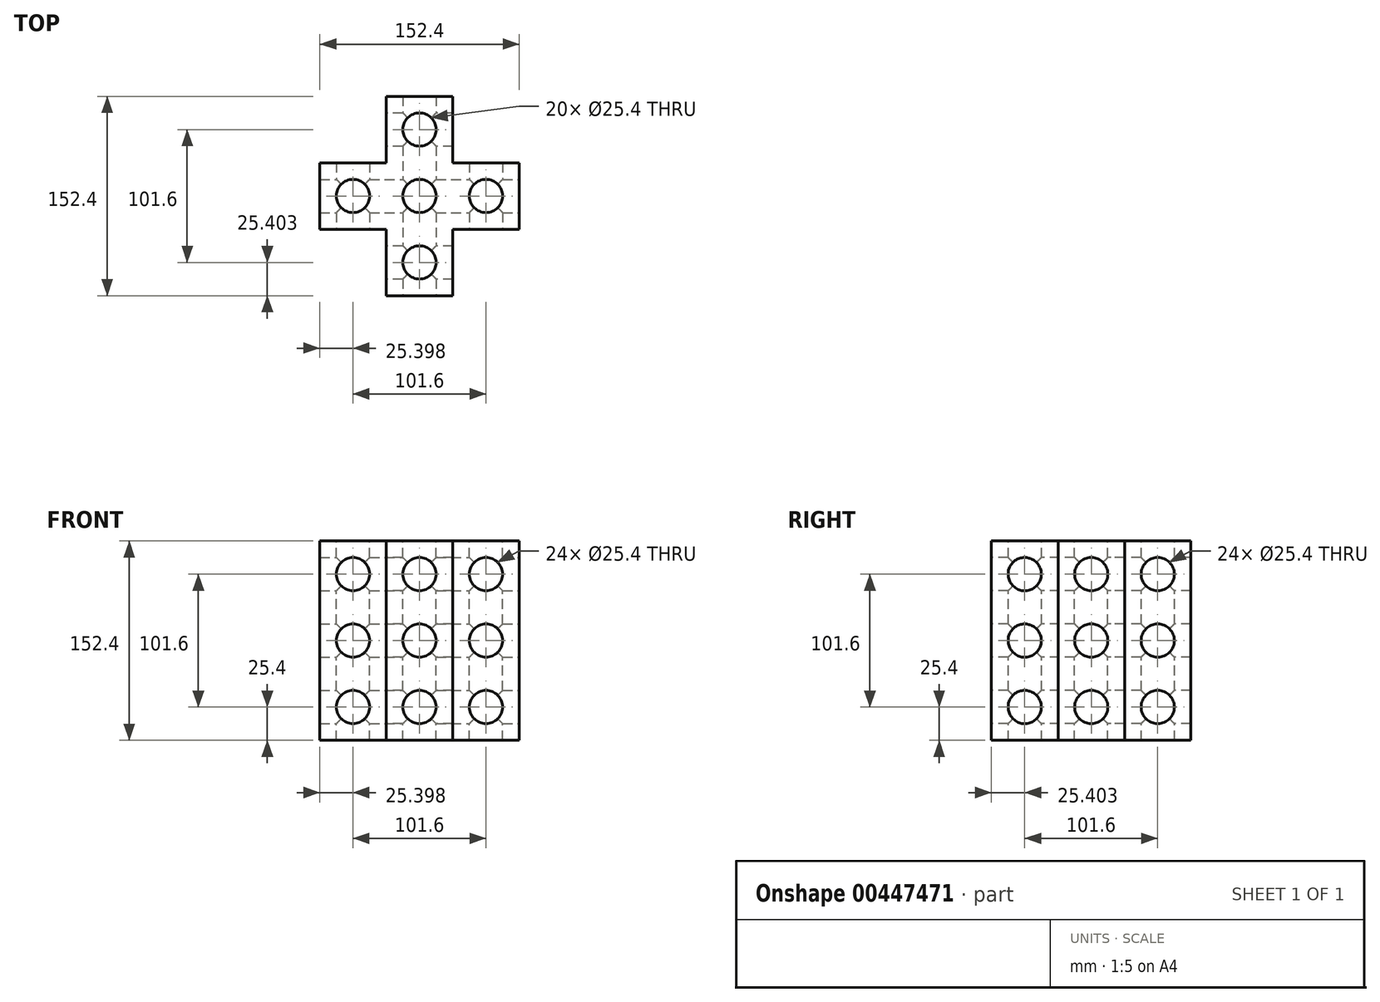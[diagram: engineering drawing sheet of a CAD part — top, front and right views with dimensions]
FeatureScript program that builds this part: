
annotation { "Feature Type Name" : "Feature", "Feature Type Description" : "" }
export const myFeature = defineFeature(function(context is Context, id is Id, definition is map)
    precondition{}
    {
        {
            var Q0;
            Q0=qCreatedBy(makeId("Top.planeOp"),FACE);
            var sketch = newSketch(context, id + "F0", { "sketchPlane" : qUnion([Q0])});
            skLineSegment(sketch, "E0", {"start": v(14.3, 102.3) * mm, "end": v(-36.5, 102.3) * mm});
            skLineSegment(sketch, "E1", {"start": v(-36.5, 102.3) * mm, "end": v(-36.5, 51.5) * mm});
            skLineSegment(sketch, "E2", {"start": v(-36.5, 51.5) * mm, "end": v(-87.3, 51.5) * mm});
            skLineSegment(sketch, "E3", {"start": v(-87.3, 51.5) * mm, "end": v(-87.3, 0.7) * mm});
            skLineSegment(sketch, "E4", {"start": v(-87.3, 0.7) * mm, "end": v(-36.5, 0.7) * mm});
            skLineSegment(sketch, "E5", {"start": v(-36.5, 0.7) * mm, "end": v(-36.5, -50.1) * mm});
            skLineSegment(sketch, "E6", {"start": v(-36.5, -50.1) * mm, "end": v(14.3, -50.1) * mm});
            skLineSegment(sketch, "E7", {"start": v(14.3, -50.1) * mm, "end": v(14.3, 0.7) * mm});
            skLineSegment(sketch, "E8", {"start": v(14.3, 0.7) * mm, "end": v(65.1, 0.7) * mm});
            skLineSegment(sketch, "E9", {"start": v(65.1, 0.7) * mm, "end": v(65.1, 51.5) * mm});
            skLineSegment(sketch, "E10", {"start": v(65.1, 51.5) * mm, "end": v(14.3, 51.5) * mm});
            skLineSegment(sketch, "E11", {"start": v(14.3, 51.5) * mm, "end": v(14.3, 102.3) * mm});
            skSolve(sketch);
        }
        {
            var Q0;
            Q0 = qSketchRegion(id + "F0", true);
            extrude(context, id + "F1", {"entities" : qUnion([Q0]), "depth" : 152.4 * mm});
        }
        {
            var Q0;
            Q0=makeQuery(id+"F1.opExtrude","SWEPT_FACE",FACE,{"disambiguationData":[OSD([sQuery(id+"F0.wireOp",EDGE,"E6")])]});
            var sketch = newSketch(context, id + "F2", { "sketchPlane" : qUnion([Q0])});
            skCircle(sketch, "E12", {"center": v(-11.1, 127) * mm, "radius": 12.7 * mm});
            skCircle(sketch, "E13", {"center": v(-11.1, 76.2) * mm, "radius": 12.7 * mm});
            skCircle(sketch, "E14", {"center": v(-11.1, 25.4) * mm, "radius": 12.7 * mm});
            skSolve(sketch);
        }
        {
            var Q0;
            Q0=sQuery(id+"F2.wireOp",VERTEX,"E12.center");
            var Q1;
            Q1=makeQuery(id+"F1.opExtrude","SWEPT_BODY",BODY,{"disambiguationData":[OSD([sQuery(id+"F0.wireOp",EDGE,"E0"),sQuery(id+"F0.wireOp",EDGE,"E1"),sQuery(id+"F0.wireOp",EDGE,"E2"),sQuery(id+"F0.wireOp",EDGE,"E3"),sQuery(id+"F0.wireOp",EDGE,"E4"),sQuery(id+"F0.wireOp",EDGE,"E5"),sQuery(id+"F0.wireOp",EDGE,"E6"),sQuery(id+"F0.wireOp",EDGE,"E7"),sQuery(id+"F0.wireOp",EDGE,"E8"),sQuery(id+"F0.wireOp",EDGE,"E9"),sQuery(id+"F0.wireOp",EDGE,"E10"),sQuery(id+"F0.wireOp",EDGE,"E11")])]});
            hole(context, id + "F3", {"style" : HoleStyle.SIMPLE, "endStyle" : HoleEndStyle.THROUGH, "holeDiameter" : 25.4 * mm, "isTappedThrough" : true, "tappedDepth" : 12.7 * mm, "tapClearance" : 3, "locations" : qUnion([Q0]), "scope" : qUnion([Q1])});
        }
        {
            var Q0;
            Q0=makeQuery(id+"F1.opExtrude","SWEPT_FACE",FACE,{"disambiguationData":[OSD([sQuery(id+"F0.wireOp",EDGE,"E6")])]});
            var sketch = newSketch(context, id + "F4", { "sketchPlane" : qUnion([Q0])});
            skCircle(sketch, "E15", {"center": v(-11.1, 76.2) * mm, "radius": 12.7 * mm});
            skSolve(sketch);
        }
        {
            var Q0;
            Q0=sQuery(id+"F4.wireOp",VERTEX,"E15.center");
            var Q1;
            Q1=makeQuery(id+"F1.opExtrude","SWEPT_BODY",BODY,{"disambiguationData":[OSD([sQuery(id+"F0.wireOp",EDGE,"E0"),sQuery(id+"F0.wireOp",EDGE,"E1"),sQuery(id+"F0.wireOp",EDGE,"E2"),sQuery(id+"F0.wireOp",EDGE,"E3"),sQuery(id+"F0.wireOp",EDGE,"E4"),sQuery(id+"F0.wireOp",EDGE,"E5"),sQuery(id+"F0.wireOp",EDGE,"E6"),sQuery(id+"F0.wireOp",EDGE,"E7"),sQuery(id+"F0.wireOp",EDGE,"E8"),sQuery(id+"F0.wireOp",EDGE,"E9"),sQuery(id+"F0.wireOp",EDGE,"E10"),sQuery(id+"F0.wireOp",EDGE,"E11")])]});
            hole(context, id + "F5", {"style" : HoleStyle.SIMPLE, "endStyle" : HoleEndStyle.THROUGH, "holeDiameter" : 25.4 * mm, "isTappedThrough" : true, "tappedDepth" : 12.7 * mm, "tapClearance" : 3, "locations" : qUnion([Q0]), "scope" : qUnion([Q1])});
        }
        {
            var Q0;
            Q0=makeQuery(id+"F1.opExtrude","SWEPT_FACE",FACE,{"disambiguationData":[OSD([sQuery(id+"F0.wireOp",EDGE,"E6")])]});
            var sketch = newSketch(context, id + "F6", { "sketchPlane" : qUnion([Q0])});
            skCircle(sketch, "E16", {"center": v(-11.1, 25.4) * mm, "radius": 12.7 * mm});
            skSolve(sketch);
        }
        {
            var Q0;
            Q0=sQuery(id+"F6.wireOp",VERTEX,"E16.center");
            var Q1;
            Q1=makeQuery(id+"F1.opExtrude","SWEPT_BODY",BODY,{"disambiguationData":[OSD([sQuery(id+"F0.wireOp",EDGE,"E0"),sQuery(id+"F0.wireOp",EDGE,"E1"),sQuery(id+"F0.wireOp",EDGE,"E2"),sQuery(id+"F0.wireOp",EDGE,"E3"),sQuery(id+"F0.wireOp",EDGE,"E4"),sQuery(id+"F0.wireOp",EDGE,"E5"),sQuery(id+"F0.wireOp",EDGE,"E6"),sQuery(id+"F0.wireOp",EDGE,"E7"),sQuery(id+"F0.wireOp",EDGE,"E8"),sQuery(id+"F0.wireOp",EDGE,"E9"),sQuery(id+"F0.wireOp",EDGE,"E10"),sQuery(id+"F0.wireOp",EDGE,"E11")])]});
            hole(context, id + "F7", {"style" : HoleStyle.SIMPLE, "endStyle" : HoleEndStyle.THROUGH, "holeDiameter" : 25.4 * mm, "isTappedThrough" : true, "tappedDepth" : 12.7 * mm, "tapClearance" : 3, "locations" : qUnion([Q0]), "scope" : qUnion([Q1])});
        }
        {
            var Q0;
            Q0=makeQuery(id+"F1.opExtrude","SWEPT_FACE",FACE,{"disambiguationData":[OSD([sQuery(id+"F0.wireOp",EDGE,"E9")])]});
            var sketch = newSketch(context, id + "F8", { "sketchPlane" : qUnion([Q0])});
            skCircle(sketch, "E17", {"center": v(26.1, 127) * mm, "radius": 12.7 * mm});
            skSolve(sketch);
        }
        {
            var Q0;
            Q0=sQuery(id+"F8.wireOp",VERTEX,"E17.center");
            var Q1;
            Q1=makeQuery(id+"F1.opExtrude","SWEPT_BODY",BODY,{"disambiguationData":[OSD([sQuery(id+"F0.wireOp",EDGE,"E0"),sQuery(id+"F0.wireOp",EDGE,"E1"),sQuery(id+"F0.wireOp",EDGE,"E2"),sQuery(id+"F0.wireOp",EDGE,"E3"),sQuery(id+"F0.wireOp",EDGE,"E4"),sQuery(id+"F0.wireOp",EDGE,"E5"),sQuery(id+"F0.wireOp",EDGE,"E6"),sQuery(id+"F0.wireOp",EDGE,"E7"),sQuery(id+"F0.wireOp",EDGE,"E8"),sQuery(id+"F0.wireOp",EDGE,"E9"),sQuery(id+"F0.wireOp",EDGE,"E10"),sQuery(id+"F0.wireOp",EDGE,"E11")])]});
            hole(context, id + "F9", {"style" : HoleStyle.SIMPLE, "endStyle" : HoleEndStyle.THROUGH, "holeDiameter" : 25.4 * mm, "isTappedThrough" : true, "tappedDepth" : 12.7 * mm, "tapClearance" : 3, "locations" : qUnion([Q0]), "scope" : qUnion([Q1])});
        }
        {
            var Q0;
            Q0=makeQuery(id+"F1.opExtrude","SWEPT_FACE",FACE,{"disambiguationData":[OSD([sQuery(id+"F0.wireOp",EDGE,"E9")])]});
            var sketch = newSketch(context, id + "F10", { "sketchPlane" : qUnion([Q0])});
            skCircle(sketch, "E18", {"center": v(26.1, 76.2) * mm, "radius": 12.7 * mm});
            skSolve(sketch);
        }
        {
            var Q0;
            Q0=sQuery(id+"F10.wireOp",VERTEX,"E18.center");
            var Q1;
            Q1=makeQuery(id+"F1.opExtrude","SWEPT_BODY",BODY,{"disambiguationData":[OSD([sQuery(id+"F0.wireOp",EDGE,"E0"),sQuery(id+"F0.wireOp",EDGE,"E1"),sQuery(id+"F0.wireOp",EDGE,"E2"),sQuery(id+"F0.wireOp",EDGE,"E3"),sQuery(id+"F0.wireOp",EDGE,"E4"),sQuery(id+"F0.wireOp",EDGE,"E5"),sQuery(id+"F0.wireOp",EDGE,"E6"),sQuery(id+"F0.wireOp",EDGE,"E7"),sQuery(id+"F0.wireOp",EDGE,"E8"),sQuery(id+"F0.wireOp",EDGE,"E9"),sQuery(id+"F0.wireOp",EDGE,"E10"),sQuery(id+"F0.wireOp",EDGE,"E11")])]});
            hole(context, id + "F11", {"style" : HoleStyle.SIMPLE, "endStyle" : HoleEndStyle.THROUGH, "holeDiameter" : 25.4 * mm, "isTappedThrough" : true, "tappedDepth" : 12.7 * mm, "tapClearance" : 3, "locations" : qUnion([Q0]), "scope" : qUnion([Q1])});
        }
        {
            var Q0;
            Q0=makeQuery(id+"F1.opExtrude","SWEPT_FACE",FACE,{"disambiguationData":[OSD([sQuery(id+"F0.wireOp",EDGE,"E9")])]});
            var sketch = newSketch(context, id + "F12", { "sketchPlane" : qUnion([Q0])});
            skCircle(sketch, "E19", {"center": v(26.1, 25.4) * mm, "radius": 12.7 * mm});
            skSolve(sketch);
        }
        {
            var Q0;
            Q0=sQuery(id+"F12.wireOp",VERTEX,"E19.center");
            var Q1;
            Q1=makeQuery(id+"F1.opExtrude","SWEPT_BODY",BODY,{"disambiguationData":[OSD([sQuery(id+"F0.wireOp",EDGE,"E0"),sQuery(id+"F0.wireOp",EDGE,"E1"),sQuery(id+"F0.wireOp",EDGE,"E2"),sQuery(id+"F0.wireOp",EDGE,"E3"),sQuery(id+"F0.wireOp",EDGE,"E4"),sQuery(id+"F0.wireOp",EDGE,"E5"),sQuery(id+"F0.wireOp",EDGE,"E6"),sQuery(id+"F0.wireOp",EDGE,"E7"),sQuery(id+"F0.wireOp",EDGE,"E8"),sQuery(id+"F0.wireOp",EDGE,"E9"),sQuery(id+"F0.wireOp",EDGE,"E10"),sQuery(id+"F0.wireOp",EDGE,"E11")])]});
            hole(context, id + "F13", {"style" : HoleStyle.SIMPLE, "endStyle" : HoleEndStyle.THROUGH, "holeDiameter" : 25.4 * mm, "isTappedThrough" : true, "tappedDepth" : 12.7 * mm, "tapClearance" : 3, "locations" : qUnion([Q0]), "scope" : qUnion([Q1])});
        }
        {
            var Q0;
            Q0=makeQuery(id+"F1.opExtrude","CAP_FACE",FACE,{"disambiguationData":[OSD([sQuery(id+"F0.wireOp",EDGE,"E0"),sQuery(id+"F0.wireOp",EDGE,"E1"),sQuery(id+"F0.wireOp",EDGE,"E2"),sQuery(id+"F0.wireOp",EDGE,"E3"),sQuery(id+"F0.wireOp",EDGE,"E4"),sQuery(id+"F0.wireOp",EDGE,"E5"),sQuery(id+"F0.wireOp",EDGE,"E6"),sQuery(id+"F0.wireOp",EDGE,"E7"),sQuery(id+"F0.wireOp",EDGE,"E8"),sQuery(id+"F0.wireOp",EDGE,"E9"),sQuery(id+"F0.wireOp",EDGE,"E10"),sQuery(id+"F0.wireOp",EDGE,"E11")])],"isStart":false});
            var sketch = newSketch(context, id + "F14", { "sketchPlane" : qUnion([Q0])});
            skCircle(sketch, "E20", {"center": v(-11.1, 26.1) * mm, "radius": 12.7 * mm});
            skSolve(sketch);
        }
        {
            var Q0;
            Q0=sQuery(id+"F14.wireOp",VERTEX,"E20.center");
            var Q1;
            Q1=makeQuery(id+"F1.opExtrude","SWEPT_BODY",BODY,{"disambiguationData":[OSD([sQuery(id+"F0.wireOp",EDGE,"E0"),sQuery(id+"F0.wireOp",EDGE,"E1"),sQuery(id+"F0.wireOp",EDGE,"E2"),sQuery(id+"F0.wireOp",EDGE,"E3"),sQuery(id+"F0.wireOp",EDGE,"E4"),sQuery(id+"F0.wireOp",EDGE,"E5"),sQuery(id+"F0.wireOp",EDGE,"E6"),sQuery(id+"F0.wireOp",EDGE,"E7"),sQuery(id+"F0.wireOp",EDGE,"E8"),sQuery(id+"F0.wireOp",EDGE,"E9"),sQuery(id+"F0.wireOp",EDGE,"E10"),sQuery(id+"F0.wireOp",EDGE,"E11")])]});
            hole(context, id + "F15", {"style" : HoleStyle.SIMPLE, "endStyle" : HoleEndStyle.THROUGH, "holeDiameter" : 25.4 * mm, "isTappedThrough" : true, "tappedDepth" : 12.7 * mm, "tapClearance" : 3, "locations" : qUnion([Q0]), "scope" : qUnion([Q1])});
        }
        {
            var Q0;
            Q0=makeQuery(id+"F1.opExtrude","CAP_FACE",FACE,{"disambiguationData":[OSD([sQuery(id+"F0.wireOp",EDGE,"E0"),sQuery(id+"F0.wireOp",EDGE,"E1"),sQuery(id+"F0.wireOp",EDGE,"E2"),sQuery(id+"F0.wireOp",EDGE,"E3"),sQuery(id+"F0.wireOp",EDGE,"E4"),sQuery(id+"F0.wireOp",EDGE,"E5"),sQuery(id+"F0.wireOp",EDGE,"E6"),sQuery(id+"F0.wireOp",EDGE,"E7"),sQuery(id+"F0.wireOp",EDGE,"E8"),sQuery(id+"F0.wireOp",EDGE,"E9"),sQuery(id+"F0.wireOp",EDGE,"E10"),sQuery(id+"F0.wireOp",EDGE,"E11")])],"isStart":false});
            var sketch = newSketch(context, id + "F16", { "sketchPlane" : qUnion([Q0])});
            skCircle(sketch, "E21", {"center": v(39.7, 26.1) * mm, "radius": 12.7 * mm});
            skCircle(sketch, "E22", {"center": v(-61.9, 26.1) * mm, "radius": 12.7 * mm});
            skSolve(sketch);
        }
        {
            var Q0;
            Q0=sQuery(id+"F16.wireOp",VERTEX,"E21.center");
            var Q1;
            Q1=sQuery(id+"F16.wireOp",VERTEX,"E22.center");
            var Q2;
            Q2=makeQuery(id+"F1.opExtrude","SWEPT_BODY",BODY,{"disambiguationData":[OSD([sQuery(id+"F0.wireOp",EDGE,"E0"),sQuery(id+"F0.wireOp",EDGE,"E1"),sQuery(id+"F0.wireOp",EDGE,"E2"),sQuery(id+"F0.wireOp",EDGE,"E3"),sQuery(id+"F0.wireOp",EDGE,"E4"),sQuery(id+"F0.wireOp",EDGE,"E5"),sQuery(id+"F0.wireOp",EDGE,"E6"),sQuery(id+"F0.wireOp",EDGE,"E7"),sQuery(id+"F0.wireOp",EDGE,"E8"),sQuery(id+"F0.wireOp",EDGE,"E9"),sQuery(id+"F0.wireOp",EDGE,"E10"),sQuery(id+"F0.wireOp",EDGE,"E11")])]});
            hole(context, id + "F17", {"style" : HoleStyle.SIMPLE, "endStyle" : HoleEndStyle.THROUGH, "holeDiameter" : 25.4 * mm, "isTappedThrough" : true, "tappedDepth" : 12.7 * mm, "tapClearance" : 3, "locations" : qUnion([Q0, Q1]), "scope" : qUnion([Q2])});
        }
        {
            var Q0;
            Q0=makeQuery(id+"F1.opExtrude","SWEPT_FACE",FACE,{"disambiguationData":[OSD([sQuery(id+"F0.wireOp",EDGE,"E8")])]});
            var sketch = newSketch(context, id + "F18", { "sketchPlane" : qUnion([Q0])});
            skCircle(sketch, "E23", {"center": v(39.7, 127) * mm, "radius": 12.7 * mm});
            skCircle(sketch, "E24", {"center": v(39.7, 76.2) * mm, "radius": 12.7 * mm});
            skCircle(sketch, "E25", {"center": v(39.7, 25.4) * mm, "radius": 12.7 * mm});
            skSolve(sketch);
        }
        {
            var Q0;
            Q0=sQuery(id+"F18.wireOp",VERTEX,"E23.center");
            var Q1;
            Q1=sQuery(id+"F18.wireOp",VERTEX,"E24.center");
            var Q2;
            Q2=sQuery(id+"F18.wireOp",VERTEX,"E25.center");
            var Q3;
            Q3=makeQuery(id+"F1.opExtrude","SWEPT_BODY",BODY,{"disambiguationData":[OSD([sQuery(id+"F0.wireOp",EDGE,"E0"),sQuery(id+"F0.wireOp",EDGE,"E1"),sQuery(id+"F0.wireOp",EDGE,"E2"),sQuery(id+"F0.wireOp",EDGE,"E3"),sQuery(id+"F0.wireOp",EDGE,"E4"),sQuery(id+"F0.wireOp",EDGE,"E5"),sQuery(id+"F0.wireOp",EDGE,"E6"),sQuery(id+"F0.wireOp",EDGE,"E7"),sQuery(id+"F0.wireOp",EDGE,"E8"),sQuery(id+"F0.wireOp",EDGE,"E9"),sQuery(id+"F0.wireOp",EDGE,"E10"),sQuery(id+"F0.wireOp",EDGE,"E11")])]});
            hole(context, id + "F19", {"style" : HoleStyle.SIMPLE, "endStyle" : HoleEndStyle.THROUGH, "holeDiameter" : 25.4 * mm, "isTappedThrough" : true, "tappedDepth" : 12.7 * mm, "tapClearance" : 3, "locations" : qUnion([Q0, Q1, Q2]), "scope" : qUnion([Q3])});
        }
        {
            var Q0;
            Q0=makeQuery(id+"F1.opExtrude","SWEPT_FACE",FACE,{"disambiguationData":[OSD([sQuery(id+"F0.wireOp",EDGE,"E4")])]});
            var sketch = newSketch(context, id + "F20", { "sketchPlane" : qUnion([Q0])});
            skCircle(sketch, "E26", {"center": v(-61.9, 127) * mm, "radius": 12.7 * mm});
            skCircle(sketch, "E27", {"center": v(-61.9, 76.2) * mm, "radius": 12.7 * mm});
            skCircle(sketch, "E28", {"center": v(-61.9, 25.4) * mm, "radius": 12.7 * mm});
            skSolve(sketch);
        }
        {
            var Q0;
            Q0=sQuery(id+"F20.wireOp",VERTEX,"E26.center");
            var Q1;
            Q1=sQuery(id+"F20.wireOp",VERTEX,"E27.center");
            var Q2;
            Q2=sQuery(id+"F20.wireOp",VERTEX,"E28.center");
            var Q3;
            Q3=makeQuery(id+"F1.opExtrude","SWEPT_BODY",BODY,{"disambiguationData":[OSD([sQuery(id+"F0.wireOp",EDGE,"E0"),sQuery(id+"F0.wireOp",EDGE,"E1"),sQuery(id+"F0.wireOp",EDGE,"E2"),sQuery(id+"F0.wireOp",EDGE,"E3"),sQuery(id+"F0.wireOp",EDGE,"E4"),sQuery(id+"F0.wireOp",EDGE,"E5"),sQuery(id+"F0.wireOp",EDGE,"E6"),sQuery(id+"F0.wireOp",EDGE,"E7"),sQuery(id+"F0.wireOp",EDGE,"E8"),sQuery(id+"F0.wireOp",EDGE,"E9"),sQuery(id+"F0.wireOp",EDGE,"E10"),sQuery(id+"F0.wireOp",EDGE,"E11")])]});
            hole(context, id + "F21", {"style" : HoleStyle.SIMPLE, "endStyle" : HoleEndStyle.THROUGH, "holeDiameter" : 25.4 * mm, "isTappedThrough" : true, "tappedDepth" : 12.7 * mm, "tapClearance" : 3, "locations" : qUnion([Q0, Q1, Q2]), "scope" : qUnion([Q3])});
        }
        {
            var Q0;
            Q0=makeQuery(id+"F1.opExtrude","SWEPT_FACE",FACE,{"disambiguationData":[OSD([sQuery(id+"F0.wireOp",EDGE,"E5")])]});
            var sketch = newSketch(context, id + "F22", { "sketchPlane" : qUnion([Q0])});
            skCircle(sketch, "E29", {"center": v(24.7, 127) * mm, "radius": 12.7 * mm});
            skCircle(sketch, "E30", {"center": v(24.7, 76.2) * mm, "radius": 12.7 * mm});
            skCircle(sketch, "E31", {"center": v(24.7, 25.4) * mm, "radius": 12.7 * mm});
            skCircle(sketch, "E32", {"center": v(-76.9, 127) * mm, "radius": 12.7 * mm});
            skCircle(sketch, "E33", {"center": v(-76.9, 76.2) * mm, "radius": 12.7 * mm});
            skCircle(sketch, "E34", {"center": v(-76.9, 25.4) * mm, "radius": 12.7 * mm});
            skSolve(sketch);
        }
        {
            var Q0;
            Q0=sQuery(id+"F22.wireOp",VERTEX,"E29.center");
            var Q1;
            Q1=sQuery(id+"F22.wireOp",VERTEX,"E30.center");
            var Q2;
            Q2=sQuery(id+"F22.wireOp",VERTEX,"E31.center");
            var Q3;
            Q3=sQuery(id+"F22.wireOp",VERTEX,"E32.center");
            var Q4;
            Q4=sQuery(id+"F22.wireOp",VERTEX,"E33.center");
            var Q5;
            Q5=sQuery(id+"F22.wireOp",VERTEX,"E34.center");
            var Q6;
            Q6=makeQuery(id+"F1.opExtrude","SWEPT_BODY",BODY,{"disambiguationData":[OSD([sQuery(id+"F0.wireOp",EDGE,"E0"),sQuery(id+"F0.wireOp",EDGE,"E1"),sQuery(id+"F0.wireOp",EDGE,"E2"),sQuery(id+"F0.wireOp",EDGE,"E3"),sQuery(id+"F0.wireOp",EDGE,"E4"),sQuery(id+"F0.wireOp",EDGE,"E5"),sQuery(id+"F0.wireOp",EDGE,"E6"),sQuery(id+"F0.wireOp",EDGE,"E7"),sQuery(id+"F0.wireOp",EDGE,"E8"),sQuery(id+"F0.wireOp",EDGE,"E9"),sQuery(id+"F0.wireOp",EDGE,"E10"),sQuery(id+"F0.wireOp",EDGE,"E11")])]});
            hole(context, id + "F23", {"style" : HoleStyle.SIMPLE, "endStyle" : HoleEndStyle.THROUGH, "holeDiameter" : 25.4 * mm, "isTappedThrough" : true, "tappedDepth" : 12.7 * mm, "tapClearance" : 3, "locations" : qUnion([Q0, Q1, Q2, Q3, Q4, Q5]), "scope" : qUnion([Q6])});
        }
        {
            var Q0;
            Q0=makeQuery(id+"F1.opExtrude","CAP_FACE",FACE,{"disambiguationData":[OSD([sQuery(id+"F0.wireOp",EDGE,"E0"),sQuery(id+"F0.wireOp",EDGE,"E1"),sQuery(id+"F0.wireOp",EDGE,"E2"),sQuery(id+"F0.wireOp",EDGE,"E3"),sQuery(id+"F0.wireOp",EDGE,"E4"),sQuery(id+"F0.wireOp",EDGE,"E5"),sQuery(id+"F0.wireOp",EDGE,"E6"),sQuery(id+"F0.wireOp",EDGE,"E7"),sQuery(id+"F0.wireOp",EDGE,"E8"),sQuery(id+"F0.wireOp",EDGE,"E9"),sQuery(id+"F0.wireOp",EDGE,"E10"),sQuery(id+"F0.wireOp",EDGE,"E11")])],"isStart":false});
            var sketch = newSketch(context, id + "F24", { "sketchPlane" : qUnion([Q0])});
            skCircle(sketch, "E35", {"center": v(-11.1, 76.9) * mm, "radius": 12.7 * mm});
            skCircle(sketch, "E36", {"center": v(-11.1, -24.7) * mm, "radius": 12.7 * mm});
            skSolve(sketch);
        }
        {
            var Q0;
            Q0=sQuery(id+"F24.wireOp",VERTEX,"E35.center");
            var Q1;
            Q1=sQuery(id+"F24.wireOp",VERTEX,"E36.center");
            var Q2;
            Q2=makeQuery(id+"F1.opExtrude","SWEPT_BODY",BODY,{"disambiguationData":[OSD([sQuery(id+"F0.wireOp",EDGE,"E0"),sQuery(id+"F0.wireOp",EDGE,"E1"),sQuery(id+"F0.wireOp",EDGE,"E2"),sQuery(id+"F0.wireOp",EDGE,"E3"),sQuery(id+"F0.wireOp",EDGE,"E4"),sQuery(id+"F0.wireOp",EDGE,"E5"),sQuery(id+"F0.wireOp",EDGE,"E6"),sQuery(id+"F0.wireOp",EDGE,"E7"),sQuery(id+"F0.wireOp",EDGE,"E8"),sQuery(id+"F0.wireOp",EDGE,"E9"),sQuery(id+"F0.wireOp",EDGE,"E10"),sQuery(id+"F0.wireOp",EDGE,"E11")])]});
            hole(context, id + "F25", {"style" : HoleStyle.SIMPLE, "endStyle" : HoleEndStyle.THROUGH, "holeDiameter" : 25.4 * mm, "isTappedThrough" : true, "tappedDepth" : 12.7 * mm, "tapClearance" : 3, "locations" : qUnion([Q0, Q1]), "scope" : qUnion([Q2])});
        }
    });
